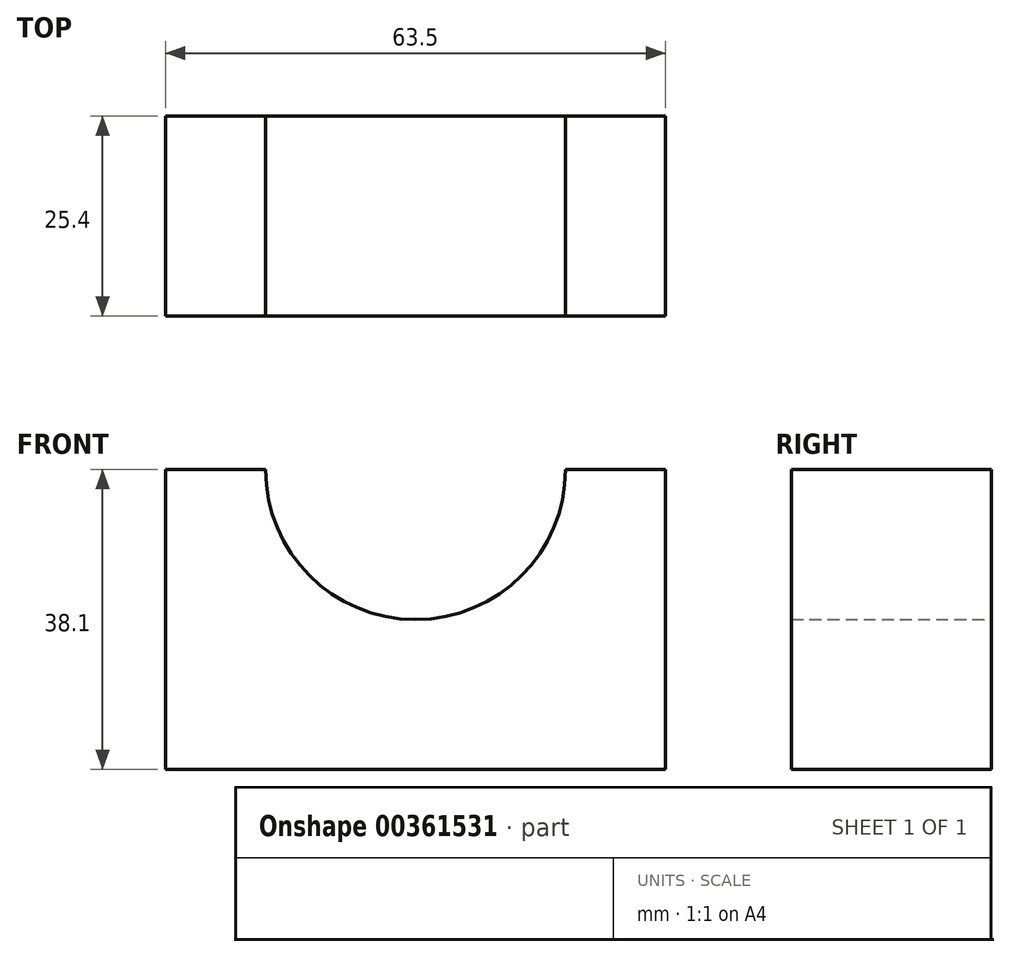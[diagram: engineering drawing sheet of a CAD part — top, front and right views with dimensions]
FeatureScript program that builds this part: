
annotation { "Feature Type Name" : "Feature", "Feature Type Description" : "" }
export const myFeature = defineFeature(function(context is Context, id is Id, definition is map)
    precondition{}
    {
        {
            var Q0;
            Q0=qCreatedBy(makeId("Front.planeOp"),FACE);
            var sketch = newSketch(context, id + "F0", { "sketchPlane" : qUnion([Q0])});
            skLineSegment(sketch, "E0", {"start": v(0, 38.1) * mm, "end": v(0, 0) * mm});
            skLineSegment(sketch, "E1", {"start": v(0, 0) * mm, "end": v(63.5, 0) * mm});
            skLineSegment(sketch, "E2", {"start": v(63.5, 0) * mm, "end": v(63.5, 38.1) * mm});
            skLineSegment(sketch, "E3", {"start": v(63.5, 38.1) * mm, "end": v(50.8, 38.1) * mm});
            skLineSegment(sketch, "E4", {"start": v(0, 38.1) * mm, "end": v(12.7, 38.1) * mm});
            skArc(sketch, "E5", {"start": v(12.7, 38.1) * mm, "mid": v(31.75, 19.05) * mm, "end": v(50.8, 38.1) * mm});
            skSolve(sketch);
        }
        {
            var Q0;
            Q0 = qSketchRegion(id + "F0", true);
            extrude(context, id + "F1", {"entities" : qUnion([Q0]), "depth" : 25.4 * mm});
        }
    });
